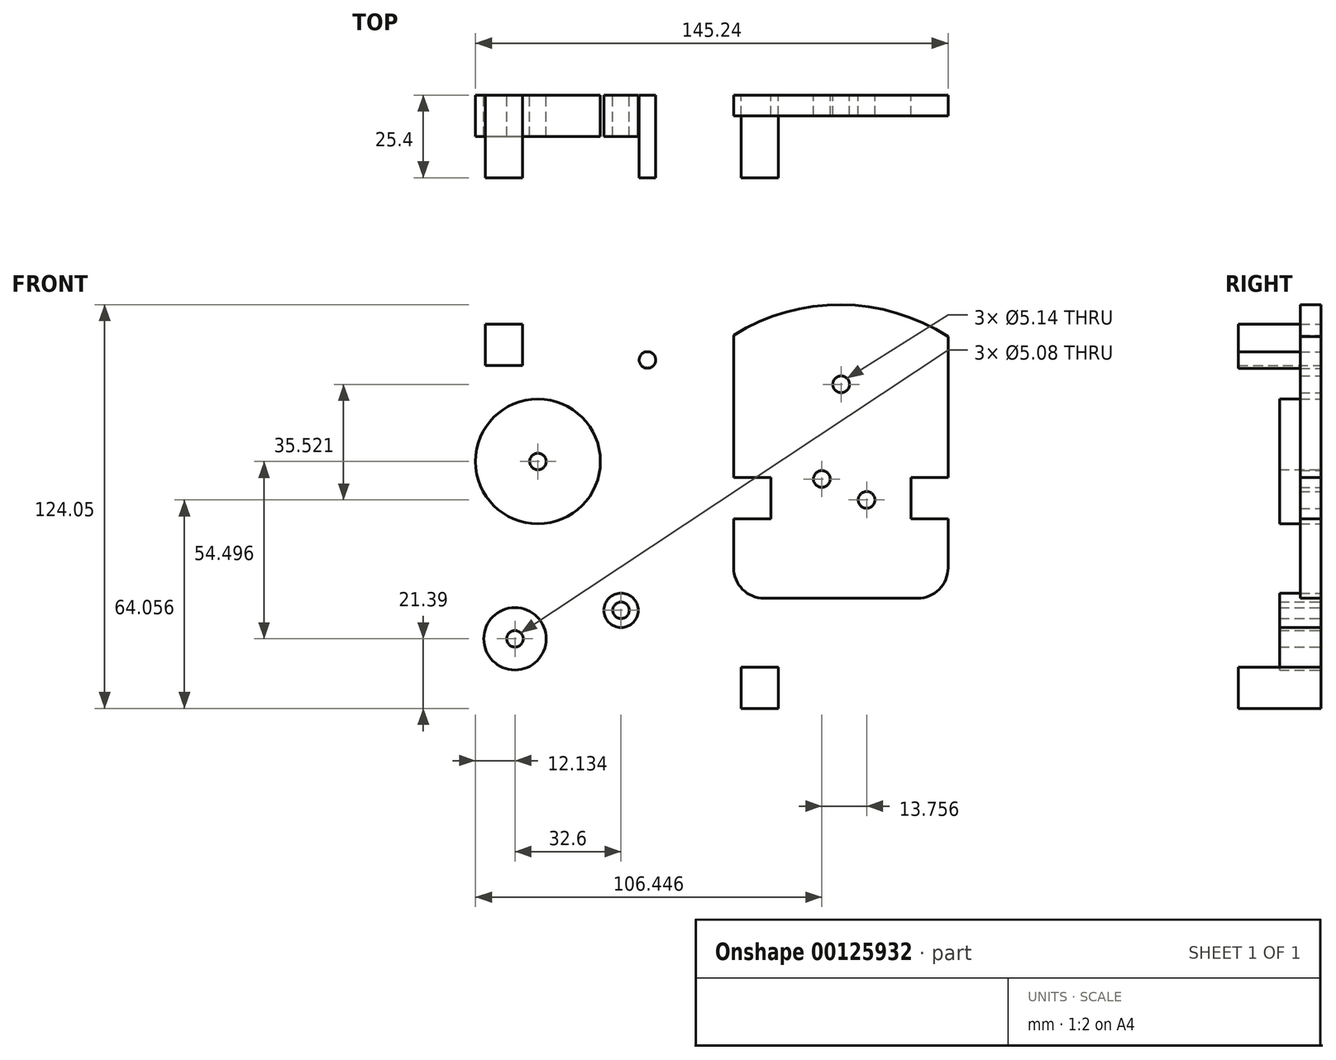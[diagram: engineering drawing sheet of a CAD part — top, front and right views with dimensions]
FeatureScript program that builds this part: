
annotation { "Feature Type Name" : "Feature", "Feature Type Description" : "" }
export const myFeature = defineFeature(function(context is Context, id is Id, definition is map)
    precondition{}
    {
        {
            var Q0;
            Q0=qCreatedBy(makeId("Front.planeOp"),FACE);
            var sketch = newSketch(context, id + "F0", { "sketchPlane" : qUnion([Q0])});
            skCircle(sketch, "E0", {"center": v(-49.4, 27.94) * mm, "radius": 19.19 * mm});
            skCircle(sketch, "E1", {"center": v(-56.46, -26.56) * mm, "radius": 9.59 * mm});
            skCircle(sketch, "E2", {"center": v(-23.86, -17.8) * mm, "radius": 5.26 * mm});
            skCircle(sketch, "E3", {"center": v(-49.4, 27.94) * mm, "radius": 2.54 * mm});
            skCircle(sketch, "E4", {"center": v(-56.46, -26.56) * mm, "radius": 2.54 * mm});
            skCircle(sketch, "E5", {"center": v(-23.86, -17.8) * mm, "radius": 2.54 * mm});
            skSolve(sketch);
        }
        {
            var Q0;
            Q0=qSketchRegion(id+"F0",true);
            extrude(context, id + "F1", {"entities" : qUnion([Q0]), "depth" : 12.7 * mm});
        }
        {
            var Q0;
            Q0=qCreatedBy(makeId("Front.planeOp"),FACE);
            var sketch = newSketch(context, id + "F2", { "sketchPlane" : qUnion([Q0])});
            skLineSegment(sketch, "E6", {"start": v(10.73, -4.76) * mm, "end": v(10.73, 10.27) * mm});
            skLineSegment(sketch, "E7", {"start": v(10.73, 10.27) * mm, "end": v(22.16, 10.27) * mm});
            skLineSegment(sketch, "E8", {"start": v(22.16, 10.27) * mm, "end": v(22.16, 22.97) * mm});
            skLineSegment(sketch, "E9", {"start": v(22.16, 22.97) * mm, "end": v(10.73, 22.97) * mm});
            skLineSegment(sketch, "E10", {"start": v(10.73, 22.97) * mm, "end": v(10.73, 66.71) * mm});
            skLineSegment(sketch, "E11", {"start": v(76.65, 66.28) * mm, "end": v(76.65, 22.97) * mm});
            skLineSegment(sketch, "E12", {"start": v(76.65, 22.97) * mm, "end": v(65.22, 22.97) * mm});
            skLineSegment(sketch, "E13", {"start": v(65.22, 22.97) * mm, "end": v(65.22, 10.27) * mm});
            skLineSegment(sketch, "E14", {"start": v(65.22, 10.27) * mm, "end": v(76.65, 10.27) * mm});
            skLineSegment(sketch, "E15", {"start": v(76.65, 10.27) * mm, "end": v(76.65, -4.76) * mm});
            skLineSegment(sketch, "E16", {"start": v(67.29, -14.11) * mm, "end": v(20.1, -14.11) * mm});
            skArc(sketch, "E17", {"start": v(76.65, 66.28) * mm, "mid": v(43.75, 76.1) * mm, "end": v(10.73, 66.71) * mm});
            skPoint(sketch, "E18.visualSharp", {"position": v(10.73, -14.11) * mm});
            skArc(sketch, "E18.filletArc", {"start": v(10.73, -4.76) * mm, "mid": v(13.47, -11.37) * mm, "end": v(20.1, -14.11) * mm});
            skPoint(sketch, "E19.visualSharp", {"position": v(76.65, -14.11) * mm});
            skArc(sketch, "E19.filletArc", {"start": v(67.29, -14.11) * mm, "mid": v(73.9, -11.37) * mm, "end": v(76.65, -4.76) * mm});
            skCircle(sketch, "E20", {"center": v(43.78, 51.63) * mm, "radius": 2.57 * mm});
            skCircle(sketch, "E21", {"center": v(37.86, 22.55) * mm, "radius": 2.57 * mm});
            skCircle(sketch, "E22", {"center": v(51.61, 16.1) * mm, "radius": 2.57 * mm});
            skSolve(sketch);
        }
        {
            var Q0;
            Q0=qSketchRegion(id+"F2",true);
            extrude(context, id + "F3", {"entities" : qUnion([Q0]), "depth" : 6.35 * mm});
        }
        {
            var Q0;
            Q0=qCreatedBy(makeId("Front.planeOp"),FACE);
            var sketch = newSketch(context, id + "F4", { "sketchPlane" : qUnion([Q0])});
            skCircle(sketch, "E23", {"center": v(-15.75, 59.12) * mm, "radius": 2.54 * mm});
            skSolve(sketch);
        }
        {
            var Q0;
            Q0=qSketchRegion(id+"F4",true);
            extrude(context, id + "F5", {"entities" : qUnion([Q0]), "depth" : 25.4 * mm});
        }
        {
            var Q0;
            Q0=qCreatedBy(makeId("Front.planeOp"),FACE);
            var sketch = newSketch(context, id + "F6", { "sketchPlane" : qUnion([Q0])});
            skLineSegment(sketch, "E24.bottom", {"start": v(-65.6, 70.13) * mm, "end": v(-54.17, 70.13) * mm});
            skLineSegment(sketch, "E24.top", {"start": v(-65.6, 57.43) * mm, "end": v(-54.17, 57.43) * mm});
            skLineSegment(sketch, "E24.left", {"start": v(-65.6, 70.13) * mm, "end": v(-65.6, 57.43) * mm});
            skLineSegment(sketch, "E24.right", {"start": v(-54.17, 70.13) * mm, "end": v(-54.17, 57.43) * mm});
            skLineSegment(sketch, "E25.bottom", {"start": v(13.02, -35.25) * mm, "end": v(24.45, -35.25) * mm});
            skLineSegment(sketch, "E25.top", {"start": v(13.02, -47.95) * mm, "end": v(24.45, -47.95) * mm});
            skLineSegment(sketch, "E25.left", {"start": v(13.02, -35.25) * mm, "end": v(13.02, -47.95) * mm});
            skLineSegment(sketch, "E25.right", {"start": v(24.45, -35.25) * mm, "end": v(24.45, -47.95) * mm});
            skSolve(sketch);
        }
        {
            var Q0;
            Q0=qSketchRegion(id+"F6",true);
            extrude(context, id + "F7", {"entities" : qUnion([Q0]), "depth" : 25.4 * mm});
        }
    });
